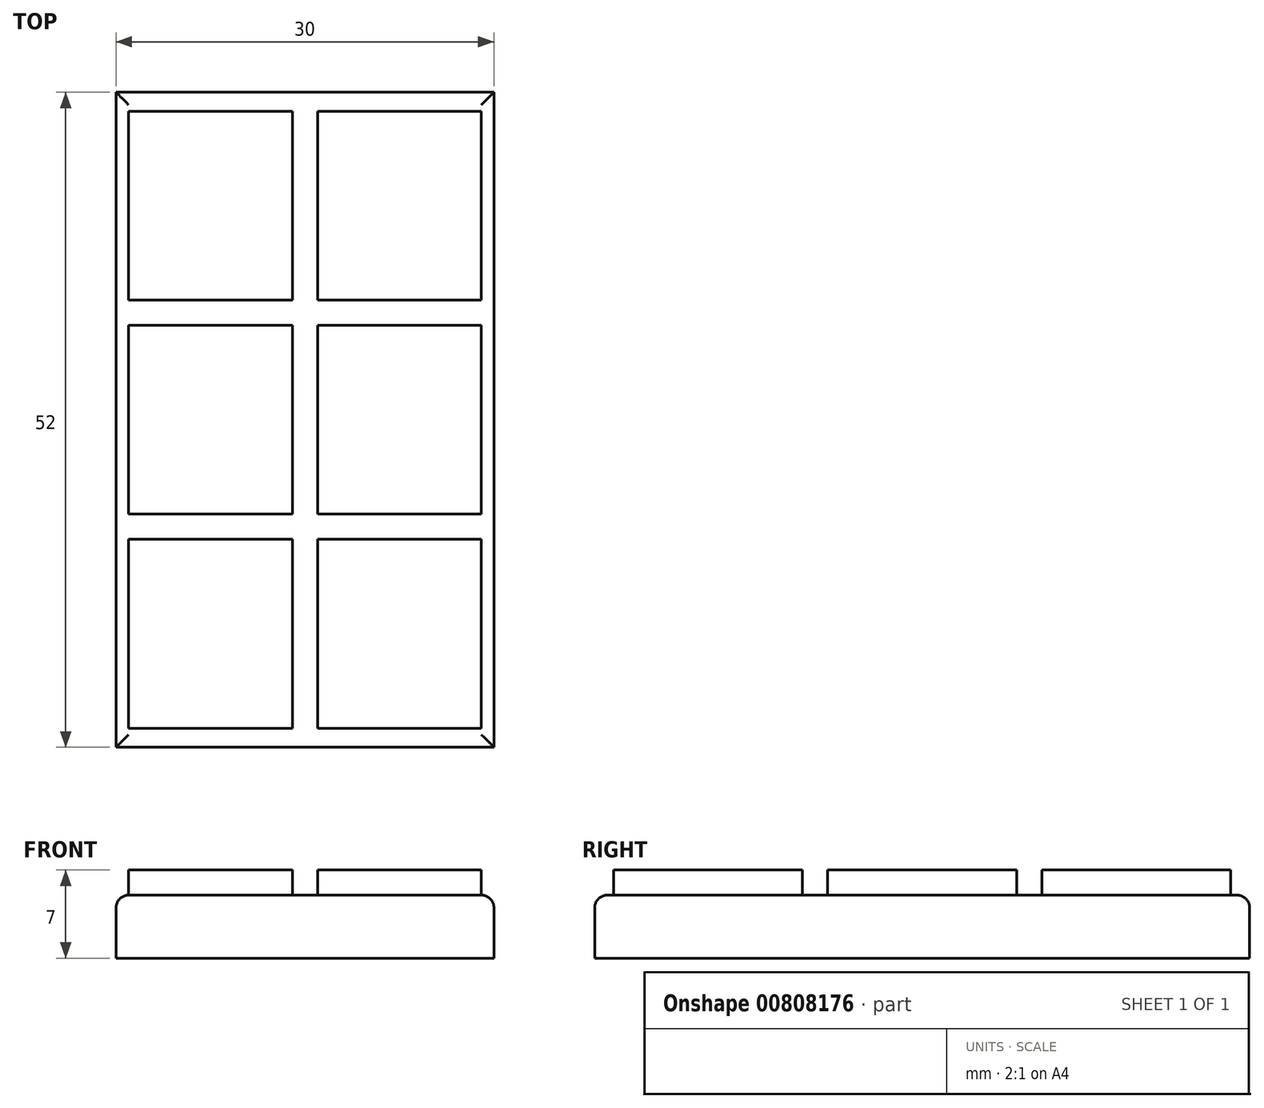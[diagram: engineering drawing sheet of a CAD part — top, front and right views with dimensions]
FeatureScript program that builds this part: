
annotation { "Feature Type Name" : "Feature", "Feature Type Description" : "" }
export const myFeature = defineFeature(function(context is Context, id is Id, definition is map)
    precondition{}
    {
        {
            var Q0;
            Q0=qCreatedBy(makeId("Top.planeOp"),FACE);
            var sketch = newSketch(context, id + "F0", { "sketchPlane" : qUnion([Q0])});
            skLineSegment(sketch, "E0.bottom", {"start": v(15, 26) * mm, "end": v(-15, 26) * mm});
            skLineSegment(sketch, "E0.top", {"start": v(15, -26) * mm, "end": v(-15, -26) * mm});
            skLineSegment(sketch, "E0.left", {"start": v(15, 26) * mm, "end": v(15, -26) * mm});
            skLineSegment(sketch, "E0.right", {"start": v(-15, 26) * mm, "end": v(-15, -26) * mm});
            skPoint(sketch, "E0.middle", {"position": v(0, 0) * mm});
            skPoint(sketch, "E1", {"position": v(-7.5, -26) * mm});
            skPoint(sketch, "E2", {"position": v(7.5, -26) * mm});
            skLineSegment(sketch, "E3", {"start": v(-7.5, 26) * mm, "end": v(-7.5, -26) * mm});
            skLineSegment(sketch, "E4", {"start": v(7.5, 26) * mm, "end": v(7.5, -26) * mm});
            skPoint(sketch, "E5", {"position": v(-7.5, -17) * mm});
            skLineSegment(sketch, "E6.bottom", {"start": v(-14, -9.5) * mm, "end": v(-1, -9.5) * mm});
            skLineSegment(sketch, "E6.top", {"start": v(-14, -24.5) * mm, "end": v(-1, -24.5) * mm});
            skLineSegment(sketch, "E6.left", {"start": v(-14, -9.5) * mm, "end": v(-14, -24.5) * mm});
            skLineSegment(sketch, "E6.right", {"start": v(-1, -9.5) * mm, "end": v(-1, -24.5) * mm});
            skPoint(sketch, "E7", {"position": v(-7.5, 0) * mm});
            skLineSegment(sketch, "E8.bottom", {"start": v(-14, -7.5) * mm, "end": v(-1, -7.5) * mm});
            skLineSegment(sketch, "E8.top", {"start": v(-14, 7.5) * mm, "end": v(-1, 7.5) * mm});
            skLineSegment(sketch, "E8.left", {"start": v(-14, -7.5) * mm, "end": v(-14, 7.5) * mm});
            skLineSegment(sketch, "E8.right", {"start": v(-1, -7.5) * mm, "end": v(-1, 7.5) * mm});
            skPoint(sketch, "E9", {"position": v(-7.5, 17) * mm});
            skLineSegment(sketch, "E10.bottom", {"start": v(-14, 9.5) * mm, "end": v(-1, 9.5) * mm});
            skLineSegment(sketch, "E10.top", {"start": v(-14, 24.5) * mm, "end": v(-1, 24.5) * mm});
            skLineSegment(sketch, "E10.left", {"start": v(-14, 9.5) * mm, "end": v(-14, 24.5) * mm});
            skLineSegment(sketch, "E10.right", {"start": v(-1, 9.5) * mm, "end": v(-1, 24.5) * mm});
            skPoint(sketch, "E11.MirrorP", {"position": v(7.5, 0) * mm});
            skPoint(sketch, "E12.MirrorP", {"position": v(7.5, 17) * mm});
            skPoint(sketch, "E13.MirrorP", {"position": v(7.5, -17) * mm});
            skLineSegment(sketch, "E14.MirrorCS", {"start": v(1, 9.5) * mm, "end": v(1, 24.5) * mm});
            skLineSegment(sketch, "E15.MirrorCS", {"start": v(14, -24.5) * mm, "end": v(1, -24.5) * mm});
            skLineSegment(sketch, "E16.MirrorCS", {"start": v(14, -7.5) * mm, "end": v(14, 7.5) * mm});
            skLineSegment(sketch, "E17.MirrorCS", {"start": v(14, -9.5) * mm, "end": v(14, -24.5) * mm});
            skLineSegment(sketch, "E18.MirrorCS", {"start": v(14, 7.5) * mm, "end": v(1, 7.5) * mm});
            skLineSegment(sketch, "E19.MirrorCS", {"start": v(14, -7.5) * mm, "end": v(1, -7.5) * mm});
            skLineSegment(sketch, "E20.MirrorCS", {"start": v(1, -9.5) * mm, "end": v(1, -24.5) * mm});
            skLineSegment(sketch, "E21.MirrorCS", {"start": v(14, 9.5) * mm, "end": v(14, 24.5) * mm});
            skLineSegment(sketch, "E22.MirrorCS", {"start": v(1, -7.5) * mm, "end": v(1, 7.5) * mm});
            skLineSegment(sketch, "E23.MirrorCS", {"start": v(14, 24.5) * mm, "end": v(1, 24.5) * mm});
            skLineSegment(sketch, "E24.MirrorCS", {"start": v(14, -9.5) * mm, "end": v(1, -9.5) * mm});
            skLineSegment(sketch, "E25.MirrorCS", {"start": v(14, 9.5) * mm, "end": v(1, 9.5) * mm});
            skSolve(sketch);
        }
        {
            var Q0;
            {var subQ5=sQuery(id+"F0.wireOp",EDGE,"pftrm2m3-TY07-467e-bGAD-67Op6henBfzw.left");Q0=makeQuery(id+"F0.imprint","IMPRINT",FACE,{"disambiguationData":[TD([[makeQuery(id+"F0.imprint","IMPRINT",EDGE,{"derivedFrom":subQ5}),-1.0]])]});}
            var Q1;
            {var subQ5=sQuery(id+"F0.wireOp",EDGE,"pftrm2m3-TY07-467e-bGAD-67Op6henBfzw.right");Q1=makeQuery(id+"F0.imprint","IMPRINT",FACE,{"disambiguationData":[TD([[makeQuery(id+"F0.imprint","IMPRINT",EDGE,{"derivedFrom":subQ5}),1.0]])]});}
            var Q2;
            {var subQ5=sQuery(id+"F0.wireOp",EDGE,"E10.right");Q2=makeQuery(id+"F0.imprint","IMPRINT",FACE,{"disambiguationData":[TD([[makeQuery(id+"F0.imprint","IMPRINT",EDGE,{"derivedFrom":subQ5}),1.0]])]});}
            var Q3;
            {var subQ5=sQuery(id+"F0.wireOp",EDGE,"E10.left");Q3=makeQuery(id+"F0.imprint","IMPRINT",FACE,{"disambiguationData":[TD([[makeQuery(id+"F0.imprint","IMPRINT",EDGE,{"derivedFrom":subQ5}),-1.0]])]});}
            var Q4;
            {var subQ5=sQuery(id+"F0.wireOp",EDGE,"E8.left");Q4=makeQuery(id+"F0.imprint","IMPRINT",FACE,{"disambiguationData":[TD([[makeQuery(id+"F0.imprint","IMPRINT",EDGE,{"derivedFrom":subQ5}),-1.0]])]});}
            var Q5;
            {var subQ5=sQuery(id+"F0.wireOp",EDGE,"E8.right");Q5=makeQuery(id+"F0.imprint","IMPRINT",FACE,{"disambiguationData":[TD([[makeQuery(id+"F0.imprint","IMPRINT",EDGE,{"derivedFrom":subQ5}),1.0]])]});}
            var Q6;
            {var subQ5=sQuery(id+"F0.wireOp",EDGE,"E6.right");Q6=makeQuery(id+"F0.imprint","IMPRINT",FACE,{"disambiguationData":[TD([[makeQuery(id+"F0.imprint","IMPRINT",EDGE,{"derivedFrom":subQ5}),-1.0]])]});}
            var Q7;
            {var subQ5=sQuery(id+"F0.wireOp",EDGE,"E6.left");Q7=makeQuery(id+"F0.imprint","IMPRINT",FACE,{"disambiguationData":[TD([[makeQuery(id+"F0.imprint","IMPRINT",EDGE,{"derivedFrom":subQ5}),1.0]])]});}
            var Q8;
            {var subQ0=sQuery(id+"F0.wireOp",EDGE,"E20.MirrorCS");Q8=makeQuery(id+"F0.imprint","IMPRINT",FACE,{"disambiguationData":[TD([[makeQuery(id+"F0.imprint","IMPRINT",EDGE,{"derivedFrom":subQ0}),1.0]])]});}
            var Q9;
            {var subQ0=sQuery(id+"F0.wireOp",EDGE,"E17.MirrorCS");Q9=makeQuery(id+"F0.imprint","IMPRINT",FACE,{"disambiguationData":[TD([[makeQuery(id+"F0.imprint","IMPRINT",EDGE,{"derivedFrom":subQ0}),-1.0]])]});}
            var Q10;
            {var subQ0=sQuery(id+"F0.wireOp",EDGE,"E16.MirrorCS");Q10=makeQuery(id+"F0.imprint","IMPRINT",FACE,{"disambiguationData":[TD([[makeQuery(id+"F0.imprint","IMPRINT",EDGE,{"derivedFrom":subQ0}),1.0]])]});}
            var Q11;
            {var subQ5=sQuery(id+"F0.wireOp",EDGE,"E22.MirrorCS");Q11=makeQuery(id+"F0.imprint","IMPRINT",FACE,{"disambiguationData":[TD([[makeQuery(id+"F0.imprint","IMPRINT",EDGE,{"derivedFrom":subQ5}),-1.0]])]});}
            var Q12;
            {var subQ0=sQuery(id+"F0.wireOp",EDGE,"E14.MirrorCS");Q12=makeQuery(id+"F0.imprint","IMPRINT",FACE,{"disambiguationData":[TD([[makeQuery(id+"F0.imprint","IMPRINT",EDGE,{"derivedFrom":subQ0}),-1.0]])]});}
            var Q13;
            {var subQ5=sQuery(id+"F0.wireOp",EDGE,"E21.MirrorCS");Q13=makeQuery(id+"F0.imprint","IMPRINT",FACE,{"disambiguationData":[TD([[makeQuery(id+"F0.imprint","IMPRINT",EDGE,{"derivedFrom":subQ5}),1.0]])]});}
            var Q14;
            {var subQ0=sQuery(id+"F0.wireOp",EDGE,"E112.MirrorCS");Q14=makeQuery(id+"F0.imprint","IMPRINT",FACE,{"disambiguationData":[TD([[makeQuery(id+"F0.imprint","IMPRINT",EDGE,{"derivedFrom":subQ0}),1.0]])]});}
            var Q15;
            {var subQ0=sQuery(id+"F0.wireOp",EDGE,"E123.MirrorCS");Q15=makeQuery(id+"F0.imprint","IMPRINT",FACE,{"disambiguationData":[TD([[makeQuery(id+"F0.imprint","IMPRINT",EDGE,{"derivedFrom":subQ0}),-1.0]])]});}
            extrude(context, id + "F1", {"entities" : qUnion([Q0, Q1, Q2, Q3, Q4, Q5, Q6, Q7, Q8, Q9, Q10, Q11, Q12, Q13, Q14, Q15]), "depth" : 7 * mm, "offsetDistance" : 25 * mm});
        }
        {
            var Q0;
            {var subQ21=sQuery(id+"F0.wireOp",EDGE,"E0.right");Q0=makeQuery(id+"F0.imprint","IMPRINT",FACE,{"disambiguationData":[TD([[makeQuery(id+"F0.imprint","IMPRINT",EDGE,{"derivedFrom":subQ21}),1.0]])]});}
            var Q1;
            {var subQ33=sQuery(id+"F0.wireOp",EDGE,"E6.right");Q1=makeQuery(id+"F0.imprint","IMPRINT",FACE,{"disambiguationData":[TD([[makeQuery(id+"F0.imprint","IMPRINT",EDGE,{"derivedFrom":subQ33}),1.0]])]});}
            var Q2;
            {var subQ12=sQuery(id+"F0.wireOp",EDGE,"E16.MirrorCS");Q2=makeQuery(id+"F0.imprint","IMPRINT",FACE,{"disambiguationData":[TD([[makeQuery(id+"F0.imprint","IMPRINT",EDGE,{"derivedFrom":subQ12}),-1.0]])]});}
            extrude(context, id + "F2", {"entities" : qUnion([Q0, Q1, Q2]), "depth" : 5 * mm, "offsetDistance" : 25 * mm});
        }
        {
            var Q0;
            Q0=makeQuery(id+"F1.opExtrude","SWEPT_BODY",BODY,{"disambiguationData":[OSD([sQuery(id+"F0.wireOp",EDGE,"E14.MirrorCS"),sQuery(id+"F0.wireOp",EDGE,"E21.MirrorCS"),sQuery(id+"F0.wireOp",EDGE,"E23.MirrorCS"),sQuery(id+"F0.wireOp",EDGE,"E25.MirrorCS")])]});
            var Q1;
            Q1=makeQuery(id+"F1.opExtrude","SWEPT_BODY",BODY,{"disambiguationData":[OSD([sQuery(id+"F0.wireOp",EDGE,"E8.bottom"),sQuery(id+"F0.wireOp",EDGE,"E8.top"),sQuery(id+"F0.wireOp",EDGE,"E8.left"),sQuery(id+"F0.wireOp",EDGE,"E8.right")])]});
            var Q2;
            Q2=makeQuery(id+"F1.opExtrude","SWEPT_BODY",BODY,{"disambiguationData":[OSD([sQuery(id+"F0.wireOp",EDGE,"E6.bottom"),sQuery(id+"F0.wireOp",EDGE,"E6.top"),sQuery(id+"F0.wireOp",EDGE,"E6.left"),sQuery(id+"F0.wireOp",EDGE,"E6.right")])]});
            var Q3;
            Q3=makeQuery(id+"F2.opExtrude","SWEPT_BODY",BODY,{"disambiguationData":[OSD([sQuery(id+"F0.wireOp",EDGE,"E0.bottom"),sQuery(id+"F0.wireOp",EDGE,"E0.top"),sQuery(id+"F0.wireOp",EDGE,"E0.right"),sQuery(id+"F0.wireOp",EDGE,"E6.bottom"),sQuery(id+"F0.wireOp",EDGE,"E6.top"),sQuery(id+"F0.wireOp",EDGE,"E6.left"),sQuery(id+"F0.wireOp",EDGE,"E6.right"),sQuery(id+"F0.wireOp",EDGE,"E8.bottom"),sQuery(id+"F0.wireOp",EDGE,"E8.top"),sQuery(id+"F0.wireOp",EDGE,"E8.left"),sQuery(id+"F0.wireOp",EDGE,"E8.right"),sQuery(id+"F0.wireOp",EDGE,"E10.bottom"),sQuery(id+"F0.wireOp",EDGE,"E10.top"),sQuery(id+"F0.wireOp",EDGE,"E10.left"),sQuery(id+"F0.wireOp",EDGE,"E10.right"),sQuery(id+"F0.wireOp",EDGE,"pftrm2m3-TY07-467e-bGAD-67Op6henBfzw.bottom"),sQuery(id+"F0.wireOp",EDGE,"pftrm2m3-TY07-467e-bGAD-67Op6henBfzw.top"),sQuery(id+"F0.wireOp",EDGE,"pftrm2m3-TY07-467e-bGAD-67Op6henBfzw.left"),sQuery(id+"F0.wireOp",EDGE,"pftrm2m3-TY07-467e-bGAD-67Op6henBfzw.right"),sQuery(id+"F0.wireOp",EDGE,"8b5bf493-e67a-4c48-ac85-4f02ab1367354.MirrorCS"),sQuery(id+"F0.wireOp",EDGE,"E14.MirrorCS"),sQuery(id+"F0.wireOp",EDGE,"E15.MirrorCS"),sQuery(id+"F0.wireOp",EDGE,"E16.MirrorCS"),sQuery(id+"F0.wireOp",EDGE,"E17.MirrorCS"),sQuery(id+"F0.wireOp",EDGE,"E112.MirrorCS"),sQuery(id+"F0.wireOp",EDGE,"E0.left"),sQuery(id+"F0.wireOp",EDGE,"E18.MirrorCS"),sQuery(id+"F0.wireOp",EDGE,"E19.MirrorCS"),sQuery(id+"F0.wireOp",EDGE,"E20.MirrorCS"),sQuery(id+"F0.wireOp",EDGE,"E21.MirrorCS"),sQuery(id+"F0.wireOp",EDGE,"E121.MirrorCS"),sQuery(id+"F0.wireOp",EDGE,"E22.MirrorCS"),sQuery(id+"F0.wireOp",EDGE,"E123.MirrorCS"),sQuery(id+"F0.wireOp",EDGE,"E23.MirrorCS"),sQuery(id+"F0.wireOp",EDGE,"E24.MirrorCS"),sQuery(id+"F0.wireOp",EDGE,"E25.MirrorCS")])]});
            var Q4;
            Q4=makeQuery(id+"F1.opExtrude","SWEPT_BODY",BODY,{"disambiguationData":[OSD([sQuery(id+"F0.wireOp",EDGE,"E10.bottom"),sQuery(id+"F0.wireOp",EDGE,"E10.top"),sQuery(id+"F0.wireOp",EDGE,"E10.left"),sQuery(id+"F0.wireOp",EDGE,"E10.right")])]});
            var Q5;
            Q5=makeQuery(id+"F1.opExtrude","SWEPT_BODY",BODY,{"disambiguationData":[OSD([sQuery(id+"F0.wireOp",EDGE,"pftrm2m3-TY07-467e-bGAD-67Op6henBfzw.bottom"),sQuery(id+"F0.wireOp",EDGE,"pftrm2m3-TY07-467e-bGAD-67Op6henBfzw.top"),sQuery(id+"F0.wireOp",EDGE,"pftrm2m3-TY07-467e-bGAD-67Op6henBfzw.left"),sQuery(id+"F0.wireOp",EDGE,"pftrm2m3-TY07-467e-bGAD-67Op6henBfzw.right")])]});
            var Q6;
            Q6=makeQuery(id+"F1.opExtrude","SWEPT_BODY",BODY,{"disambiguationData":[OSD([sQuery(id+"F0.wireOp",EDGE,"8b5bf493-e67a-4c48-ac85-4f02ab1367354.MirrorCS"),sQuery(id+"F0.wireOp",EDGE,"E112.MirrorCS"),sQuery(id+"F0.wireOp",EDGE,"E121.MirrorCS"),sQuery(id+"F0.wireOp",EDGE,"E123.MirrorCS")])]});
            var Q7;
            Q7=makeQuery(id+"F1.opExtrude","SWEPT_BODY",BODY,{"disambiguationData":[OSD([sQuery(id+"F0.wireOp",EDGE,"E15.MirrorCS"),sQuery(id+"F0.wireOp",EDGE,"E17.MirrorCS"),sQuery(id+"F0.wireOp",EDGE,"E20.MirrorCS"),sQuery(id+"F0.wireOp",EDGE,"E24.MirrorCS")])]});
            var Q8;
            Q8=makeQuery(id+"F1.opExtrude","SWEPT_BODY",BODY,{"disambiguationData":[OSD([sQuery(id+"F0.wireOp",EDGE,"E16.MirrorCS"),sQuery(id+"F0.wireOp",EDGE,"E18.MirrorCS"),sQuery(id+"F0.wireOp",EDGE,"E19.MirrorCS"),sQuery(id+"F0.wireOp",EDGE,"E22.MirrorCS")])]});
            booleanBodies(context, id + "F3", {"operationType" : BooleanOperationType.UNION, "tools" : qUnion([Q0, Q1, Q2, Q3, Q4, Q5, Q6, Q7, Q8])});
        }
        {
            var Q0;
            Q0=makeQuery(id+"F2.opExtrude","CAP_EDGE",EDGE,{"disambiguationData":[OSD([sQuery(id+"F0.wireOp",EDGE,"E0.right")])],"isStart":false});
            var Q1;
            Q1=makeQuery(id+"F2.opExtrude","CAP_EDGE",EDGE,{"disambiguationData":[OSD([sQuery(id+"F0.wireOp",EDGE,"E0.top")])],"isStart":false});
            var Q2;
            Q2=makeQuery(id+"F2.opExtrude","CAP_EDGE",EDGE,{"disambiguationData":[OSD([sQuery(id+"F0.wireOp",EDGE,"E0.left")])],"isStart":false});
            var Q3;
            Q3=makeQuery(id+"F2.opExtrude","CAP_EDGE",EDGE,{"disambiguationData":[OSD([sQuery(id+"F0.wireOp",EDGE,"E0.bottom")])],"isStart":false});
            fillet(context, id + "F4", {"entities" : qUnion([Q0, Q1, Q2, Q3]), "radius" : 1 * mm, "tangentPropagation" : true, "allowEdgeOverflow" : false});
        }
    });
